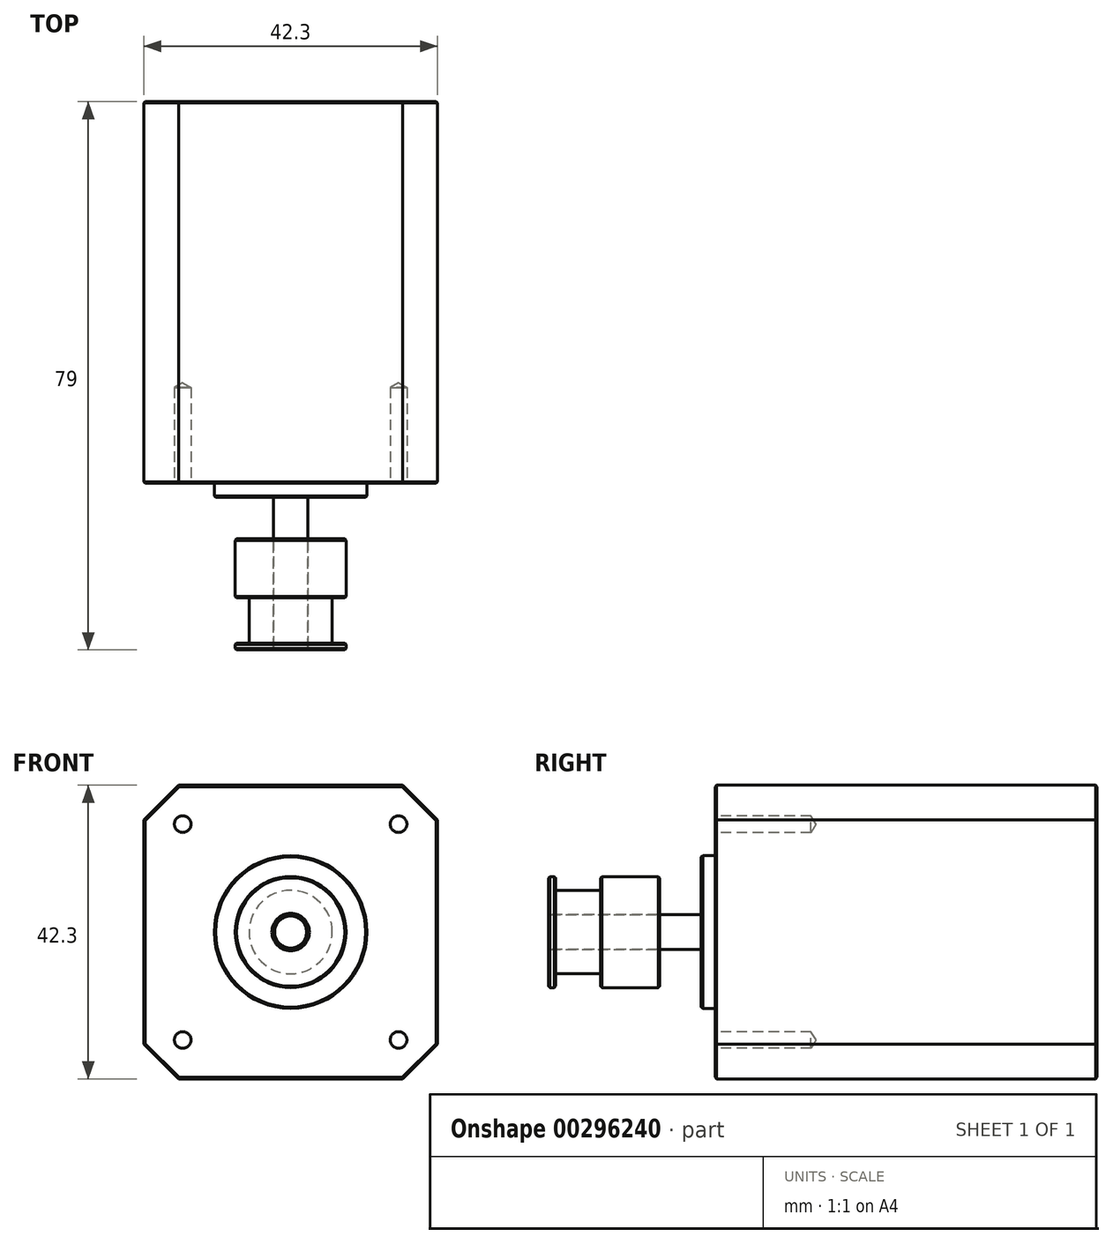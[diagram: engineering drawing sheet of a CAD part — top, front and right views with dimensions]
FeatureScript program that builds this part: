
annotation { "Feature Type Name" : "Feature", "Feature Type Description" : "" }
export const myFeature = defineFeature(function(context is Context, id is Id, definition is map)
    precondition{}
    {
        {
            var Q0;
            Q0=qCreatedBy(makeId("Front.planeOp"),FACE);
            var sketch = newSketch(context, id + "F0", { "sketchPlane" : qUnion([Q0])});
            skLineSegment(sketch, "E0.bottom", {"start": v(21.15, 21.15) * mm, "end": v(-21.15, 21.15) * mm});
            skLineSegment(sketch, "E0.top", {"start": v(21.15, -21.15) * mm, "end": v(-21.15, -21.15) * mm});
            skLineSegment(sketch, "E0.left", {"start": v(21.15, 21.15) * mm, "end": v(21.15, -21.15) * mm});
            skLineSegment(sketch, "E0.right", {"start": v(-21.15, 21.15) * mm, "end": v(-21.15, -21.15) * mm});
            skPoint(sketch, "E0.middle", {"position": v(0, 0) * mm});
            skCircle(sketch, "E1", {"center": v(0, 0) * mm, "radius": 11 * mm});
            skCircle(sketch, "E2", {"center": v(0, 0) * mm, "radius": 2.5 * mm});
            skLineSegment(sketch, "E3.bottom", {"start": v(15.55, 15.55) * mm, "end": v(-15.55, 15.55) * mm});
            skLineSegment(sketch, "E3.top", {"start": v(15.55, -15.55) * mm, "end": v(-15.55, -15.55) * mm});
            skLineSegment(sketch, "E3.left", {"start": v(15.55, 15.55) * mm, "end": v(15.55, -15.55) * mm});
            skLineSegment(sketch, "E3.right", {"start": v(-15.55, 15.55) * mm, "end": v(-15.55, -15.55) * mm});
            skSolve(sketch);
        }
        {
            var Q0;
            Q0=makeQuery(id+"F0.imprint","IMPRINT",FACE,{"disambiguationData":[TD([[makeQuery(id+"F0.imprint","IMPRINT",EDGE,{"derivedFrom":sQuery(id+"F0.wireOp",EDGE,"E1")}),1.0]])]});
            extrude(context, id + "F1", {"entities" : qUnion([Q0]), "depth" : 2 * mm});
        }
        {
            var Q0;
            Q0=makeQuery(id+"F0.imprint","IMPRINT",FACE,{"disambiguationData":[TD([[makeQuery(id+"F0.imprint","IMPRINT",EDGE,{"derivedFrom":sQuery(id+"F0.wireOp",EDGE,"E2")}),1.0]])]});
            extrude(context, id + "F2", {"entities" : qUnion([Q0]), "operationType" : NewBodyOperationType.ADD, "depth" : 24 * mm});
        }
        {
            var Q0;
            Q0=makeQuery(id+"F0.imprint","IMPRINT",FACE,{"disambiguationData":[TD([[makeQuery(id+"F0.imprint","IMPRINT",EDGE,{"derivedFrom":sQuery(id+"F0.wireOp",EDGE,"E0.bottom")}),1.0]])]});
            var Q1;
            {var subQ0=sQuery(id+"F0.wireOp",EDGE,"E2");Q1=makeQuery(id+"F2.boolean.opBoolean","MERGE",FACE,{"derivedFrom":[makeQuery(id+"F1.opExtrude","CAP_FACE",FACE,{"disambiguationData":[OSD([sQuery(id+"F0.wireOp",EDGE,"E1"),subQ0])],"isStart":true}),makeQuery(id+"F2.opExtrude","CAP_FACE",FACE,{"disambiguationData":[OSD([subQ0])],"isStart":true})]});}
            var Q2;
            Q2=makeQuery(id+"F0.imprint","IMPRINT",FACE,{"disambiguationData":[TD([[makeQuery(id+"F0.imprint","IMPRINT",EDGE,{"derivedFrom":sQuery(id+"F0.wireOp",EDGE,"E1")}),-1.0]])]});
            extrude(context, id + "F3", {"entities" : qUnion([Q0, Q1, Q2]), "operationType" : NewBodyOperationType.ADD, "oppositeDirection" : true, "depth" : 55 * mm});
        }
        {
            var Q0;
            Q0=makeQuery(id+"F3.opExtrude","SWEPT_EDGE",EDGE,{"disambiguationData":[OSD([sQuery(id+"F0.wireOp",EDGE,"E0.bottom"),sQuery(id+"F0.wireOp",EDGE,"E0.left")])]});
            var Q1;
            Q1=makeQuery(id+"F3.opExtrude","SWEPT_EDGE",EDGE,{"disambiguationData":[OSD([sQuery(id+"F0.wireOp",EDGE,"E0.top"),sQuery(id+"F0.wireOp",EDGE,"E0.left")])]});
            var Q2;
            Q2=makeQuery(id+"F3.opExtrude","SWEPT_EDGE",EDGE,{"disambiguationData":[OSD([sQuery(id+"F0.wireOp",EDGE,"E0.top"),sQuery(id+"F0.wireOp",EDGE,"E0.right")])]});
            var Q3;
            Q3=makeQuery(id+"F3.opExtrude","SWEPT_EDGE",EDGE,{"disambiguationData":[OSD([sQuery(id+"F0.wireOp",EDGE,"E0.bottom"),sQuery(id+"F0.wireOp",EDGE,"E0.right")])]});
            chamfer(context, id + "F4", {"entities" : qUnion([Q0, Q1, Q2, Q3]), "width" : 5 * mm, "tangentPropagation" : true});
        }
        {
            var Q0;
            Q0=makeQuery(id+"F1.opExtrude","CAP_EDGE",EDGE,{"disambiguationData":[OSD([sQuery(id+"F0.wireOp",EDGE,"E1")])],"isStart":false});
            var Q1;
            Q1=makeQuery(id+"F2.opExtrude","CAP_EDGE",EDGE,{"disambiguationData":[OSD([sQuery(id+"F0.wireOp",EDGE,"E2")])],"isStart":false});
            var Q2;
            {var subQ0=sQuery(id+"F0.wireOp",EDGE,"E1");Q2=makeQuery(id+"F3.boolean.opBoolean","MERGE",FACE,{"derivedFrom":[makeQuery(id+"F3.opExtrude","CAP_FACE",FACE,{"disambiguationData":[OSD([sQuery(id+"F0.wireOp",EDGE,"E0.bottom"),sQuery(id+"F0.wireOp",EDGE,"E0.top"),sQuery(id+"F0.wireOp",EDGE,"E0.left"),sQuery(id+"F0.wireOp",EDGE,"E0.right"),subQ0])],"isStart":false}),makeQuery(id+"F3.opExtrude","CAP_FACE",FACE,{"disambiguationData":[OSD([subQ0,sQuery(id+"F0.wireOp",EDGE,"E2")])],"isStart":false})]});}
            var Q3;
            Q3=makeQuery(id+"F3.opExtrude","CAP_EDGE",EDGE,{"disambiguationData":[OSD([sQuery(id+"F0.wireOp",EDGE,"E0.bottom")])],"isStart":true});
            var Q4;
            {var subQ0=sQuery(id+"F0.wireOp",EDGE,"E1");var subQ1=sQuery(id+"F0.wireOp",EDGE,"E0.left");var subQ2=sQuery(id+"F0.wireOp",EDGE,"E0.bottom");Q4=makeQuery(id+"F4.opChamfer","BLEND_EDGE",EDGE,{"blendedFrom":[makeQuery(id+"F3.opExtrude","SWEPT_EDGE",EDGE,{"disambiguationData":[OSD([subQ2,subQ1])]}),makeQuery(id+"F3.boolean.opBoolean","MERGE",FACE,{"derivedFrom":[makeQuery(id+"F3.opExtrude","CAP_FACE",FACE,{"disambiguationData":[OSD([subQ2,sQuery(id+"F0.wireOp",EDGE,"E0.top"),subQ1,sQuery(id+"F0.wireOp",EDGE,"E0.right"),subQ0])],"isStart":true}),makeQuery(id+"F3.opExtrude","CAP_FACE",FACE,{"disambiguationData":[OSD([subQ0,sQuery(id+"F0.wireOp",EDGE,"E2")])],"isStart":true})]})],"blendedInto":[makeQuery(id+"F3.boolean.opBoolean","MERGE",FACE,{"derivedFrom":[makeQuery(id+"F3.opExtrude","CAP_FACE",FACE,{"disambiguationData":[OSD([subQ2,sQuery(id+"F0.wireOp",EDGE,"E0.top"),subQ1,sQuery(id+"F0.wireOp",EDGE,"E0.right"),subQ0])],"isStart":true}),makeQuery(id+"F3.opExtrude","CAP_FACE",FACE,{"disambiguationData":[OSD([subQ0,sQuery(id+"F0.wireOp",EDGE,"E2")])],"isStart":true})]})]});}
            var Q5;
            Q5=makeQuery(id+"F3.opExtrude","CAP_EDGE",EDGE,{"disambiguationData":[OSD([sQuery(id+"F0.wireOp",EDGE,"E0.left")])],"isStart":true});
            var Q6;
            {var subQ0=sQuery(id+"F0.wireOp",EDGE,"E1");var subQ1=sQuery(id+"F0.wireOp",EDGE,"E0.left");var subQ2=sQuery(id+"F0.wireOp",EDGE,"E0.top");Q6=makeQuery(id+"F4.opChamfer","BLEND_EDGE",EDGE,{"blendedFrom":[makeQuery(id+"F3.opExtrude","SWEPT_EDGE",EDGE,{"disambiguationData":[OSD([subQ2,subQ1])]}),makeQuery(id+"F3.boolean.opBoolean","MERGE",FACE,{"derivedFrom":[makeQuery(id+"F3.opExtrude","CAP_FACE",FACE,{"disambiguationData":[OSD([sQuery(id+"F0.wireOp",EDGE,"E0.bottom"),subQ2,subQ1,sQuery(id+"F0.wireOp",EDGE,"E0.right"),subQ0])],"isStart":true}),makeQuery(id+"F3.opExtrude","CAP_FACE",FACE,{"disambiguationData":[OSD([subQ0,sQuery(id+"F0.wireOp",EDGE,"E2")])],"isStart":true})]})],"blendedInto":[makeQuery(id+"F3.boolean.opBoolean","MERGE",FACE,{"derivedFrom":[makeQuery(id+"F3.opExtrude","CAP_FACE",FACE,{"disambiguationData":[OSD([sQuery(id+"F0.wireOp",EDGE,"E0.bottom"),subQ2,subQ1,sQuery(id+"F0.wireOp",EDGE,"E0.right"),subQ0])],"isStart":true}),makeQuery(id+"F3.opExtrude","CAP_FACE",FACE,{"disambiguationData":[OSD([subQ0,sQuery(id+"F0.wireOp",EDGE,"E2")])],"isStart":true})]})]});}
            var Q7;
            Q7=makeQuery(id+"F3.opExtrude","CAP_EDGE",EDGE,{"disambiguationData":[OSD([sQuery(id+"F0.wireOp",EDGE,"E0.top")])],"isStart":true});
            var Q8;
            {var subQ0=sQuery(id+"F0.wireOp",EDGE,"E1");var subQ1=sQuery(id+"F0.wireOp",EDGE,"E0.right");var subQ2=sQuery(id+"F0.wireOp",EDGE,"E0.top");Q8=makeQuery(id+"F4.opChamfer","BLEND_EDGE",EDGE,{"blendedFrom":[makeQuery(id+"F3.opExtrude","SWEPT_EDGE",EDGE,{"disambiguationData":[OSD([subQ2,subQ1])]}),makeQuery(id+"F3.boolean.opBoolean","MERGE",FACE,{"derivedFrom":[makeQuery(id+"F3.opExtrude","CAP_FACE",FACE,{"disambiguationData":[OSD([sQuery(id+"F0.wireOp",EDGE,"E0.bottom"),subQ2,sQuery(id+"F0.wireOp",EDGE,"E0.left"),subQ1,subQ0])],"isStart":true}),makeQuery(id+"F3.opExtrude","CAP_FACE",FACE,{"disambiguationData":[OSD([subQ0,sQuery(id+"F0.wireOp",EDGE,"E2")])],"isStart":true})]})],"blendedInto":[makeQuery(id+"F3.boolean.opBoolean","MERGE",FACE,{"derivedFrom":[makeQuery(id+"F3.opExtrude","CAP_FACE",FACE,{"disambiguationData":[OSD([sQuery(id+"F0.wireOp",EDGE,"E0.bottom"),subQ2,sQuery(id+"F0.wireOp",EDGE,"E0.left"),subQ1,subQ0])],"isStart":true}),makeQuery(id+"F3.opExtrude","CAP_FACE",FACE,{"disambiguationData":[OSD([subQ0,sQuery(id+"F0.wireOp",EDGE,"E2")])],"isStart":true})]})]});}
            var Q9;
            Q9=makeQuery(id+"F3.opExtrude","CAP_EDGE",EDGE,{"disambiguationData":[OSD([sQuery(id+"F0.wireOp",EDGE,"E0.right")])],"isStart":true});
            var Q10;
            {var subQ0=sQuery(id+"F0.wireOp",EDGE,"E1");var subQ1=sQuery(id+"F0.wireOp",EDGE,"E0.right");var subQ2=sQuery(id+"F0.wireOp",EDGE,"E0.bottom");Q10=makeQuery(id+"F4.opChamfer","BLEND_EDGE",EDGE,{"blendedFrom":[makeQuery(id+"F3.opExtrude","SWEPT_EDGE",EDGE,{"disambiguationData":[OSD([subQ2,subQ1])]}),makeQuery(id+"F3.boolean.opBoolean","MERGE",FACE,{"derivedFrom":[makeQuery(id+"F3.opExtrude","CAP_FACE",FACE,{"disambiguationData":[OSD([subQ2,sQuery(id+"F0.wireOp",EDGE,"E0.top"),sQuery(id+"F0.wireOp",EDGE,"E0.left"),subQ1,subQ0])],"isStart":true}),makeQuery(id+"F3.opExtrude","CAP_FACE",FACE,{"disambiguationData":[OSD([subQ0,sQuery(id+"F0.wireOp",EDGE,"E2")])],"isStart":true})]})],"blendedInto":[makeQuery(id+"F3.boolean.opBoolean","MERGE",FACE,{"derivedFrom":[makeQuery(id+"F3.opExtrude","CAP_FACE",FACE,{"disambiguationData":[OSD([subQ2,sQuery(id+"F0.wireOp",EDGE,"E0.top"),sQuery(id+"F0.wireOp",EDGE,"E0.left"),subQ1,subQ0])],"isStart":true}),makeQuery(id+"F3.opExtrude","CAP_FACE",FACE,{"disambiguationData":[OSD([subQ0,sQuery(id+"F0.wireOp",EDGE,"E2")])],"isStart":true})]})]});}
            chamfer(context, id + "F5", {"entities" : qUnion([Q0, Q1, Q2, Q3, Q4, Q5, Q6, Q7, Q8, Q9, Q10]), "width" : 0.2 * mm, "tangentPropagation" : true});
        }
        {
            var Q0;
            Q0=sQuery(id+"F0.wireOp",VERTEX,"E3.bottom.end");
            var Q1;
            Q1=sQuery(id+"F0.wireOp",VERTEX,"E3.left.start");
            var Q2;
            Q2=sQuery(id+"F0.wireOp",VERTEX,"E3.top.start");
            var Q3;
            Q3=sQuery(id+"F0.wireOp",VERTEX,"E3.top.end");
            var Q4;
            Q4=makeQuery(id+"F1.opExtrude","SWEPT_BODY",BODY,{"disambiguationData":[OSD([sQuery(id+"F0.wireOp",EDGE,"E1"),sQuery(id+"F0.wireOp",EDGE,"E2")])]});
            hole(context, id + "F6", {"style" : HoleStyle.SIMPLE, "endStyle" : HoleEndStyle.BLIND, "standardTappedOrClearance" : lookupTablePath({ "standard" : "ISO", "engagement" : "75%", "pitch" : "0.6 mm", "size" : "M3", "type" : "Tapped" }), "standardBlindInLast" : lookupTablePath({ "standard" : "ISO", "engagement" : "75%", "pitch" : "0.6 mm", "size" : "M3", "type" : "Tapped" }), "holeDiameter" : 2.4 * mm, "showTappedDepth" : true, "holeDepth" : 13.8 * mm, "tappedDepth" : 12 * mm, "tapClearance" : 3, "locations" : qUnion([Q0, Q1, Q2, Q3]), "scope" : qUnion([Q4])});
        }
        {
            var Q0;
            Q0=makeQuery(id+"F2.opExtrude","CAP_FACE",FACE,{"disambiguationData":[OSD([sQuery(id+"F0.wireOp",EDGE,"E2")])],"isStart":false});
            var sketch = newSketch(context, id + "F7", { "sketchPlane" : qUnion([Q0])});
            skCircle(sketch, "E4", {"center": v(0, 0) * mm, "radius": 8 * mm});
            skCircle(sketch, "E5", {"center": v(0, 0) * mm, "radius": 2.5 * mm});
            skSolve(sketch);
        }
        {
            var Q0;
            Q0 = qSketchRegion(id + "F7", true);
            extrude(context, id + "F8", {"entities" : qUnion([Q0]), "oppositeDirection" : true, "depth" : 16 * mm});
        }
        {
            var Q0;
            Q0=qCreatedBy(makeId("Right.planeOp"),FACE);
            var sketch = newSketch(context, id + "F9", { "sketchPlane" : qUnion([Q0])});
            skLineSegment(sketch, "E6.0", {"start": v(-24, -8) * mm, "end": v(-24, 8) * mm});
            skLineSegment(sketch, "E7", {"start": v(-24, 8) * mm, "end": v(-23, 8) * mm});
            skLineSegment(sketch, "E8", {"start": v(-23, 8) * mm, "end": v(-23, 6) * mm});
            skLineSegment(sketch, "E9", {"start": v(-23, 6) * mm, "end": v(-16.5, 6) * mm});
            skLineSegment(sketch, "E10", {"start": v(-16.5, 6) * mm, "end": v(-16.5, 8) * mm});
            skLineSegment(sketch, "E11", {"start": v(-16.5, 8) * mm, "end": v(-23, 8) * mm});
            skSolve(sketch);
        }
        {
            var Q0;
            Q0 = qSketchRegion(id + "F9", true);
            var Q1;
            {var subQ0=sQuery(id+"F0.wireOp",EDGE,"E2");Q1=makeQuery(id+"F5.opChamfer","BLEND_EDGE",EDGE,{"blendedFrom":[makeQuery(id+"F2.opExtrude","CAP_EDGE",EDGE,{"disambiguationData":[OSD([subQ0])],"isStart":false}),makeQuery(id+"F2.opExtrude","CAP_FACE",FACE,{"disambiguationData":[OSD([subQ0])],"isStart":false})],"blendedInto":[makeQuery(id+"F2.opExtrude","CAP_FACE",FACE,{"disambiguationData":[OSD([subQ0])],"isStart":false})]});}
            revolve(context, id + "F10", {"operationType" : NewBodyOperationType.REMOVE, "entities" : qUnion([Q0]), "axis" : qUnion([Q1]), "revolveType" : RevolveType.FULL, "oppositeDirection" : true});
        }
        {
            var Q0;
            Q0=makeQuery(id+"F8.opExtrude","CAP_FACE",FACE,{"disambiguationData":[OSD([sQuery(id+"F7.wireOp",EDGE,"E4"),sQuery(id+"F7.wireOp",EDGE,"E5")])],"isStart":true});
            var Q1;
            Q1=makeQuery(id+"F10.boolean.opBoolean","COPY",EDGE,{"derivedFrom":makeQuery(id+"F10.opRevolve","SWEPT_EDGE",EDGE,{"disambiguationData":[OSD([sQuery(id+"F9.wireOp",EDGE,"E8"),sQuery(id+"F9.wireOp",EDGE,"E11")])]})});
            var Q2;
            {var subQ0=sQuery(id+"F7.wireOp",EDGE,"E4");Q2=makeQuery(id+"F10.boolean.opBoolean","SPLIT",FACE,{"disambiguationData":[TD([makeQuery(id+"F10.opRevolve","SWEPT_FACE",FACE,{"disambiguationData":[OSD([sQuery(id+"F9.wireOp",EDGE,"E10")])]})])],"derivedFrom":makeQuery(id+"F8.opExtrude","SWEPT_FACE",FACE,{"disambiguationData":[OSD([subQ0])]})});}
            var Q3;
            Q3=makeQuery(id+"F8.opExtrude","CAP_EDGE",EDGE,{"disambiguationData":[OSD([sQuery(id+"F7.wireOp",EDGE,"E5")])],"isStart":false});
            chamfer(context, id + "F11", {"entities" : qUnion([Q0, Q1, Q2, Q3]), "width" : 0.2 * mm, "tangentPropagation" : true});
        }
    });
